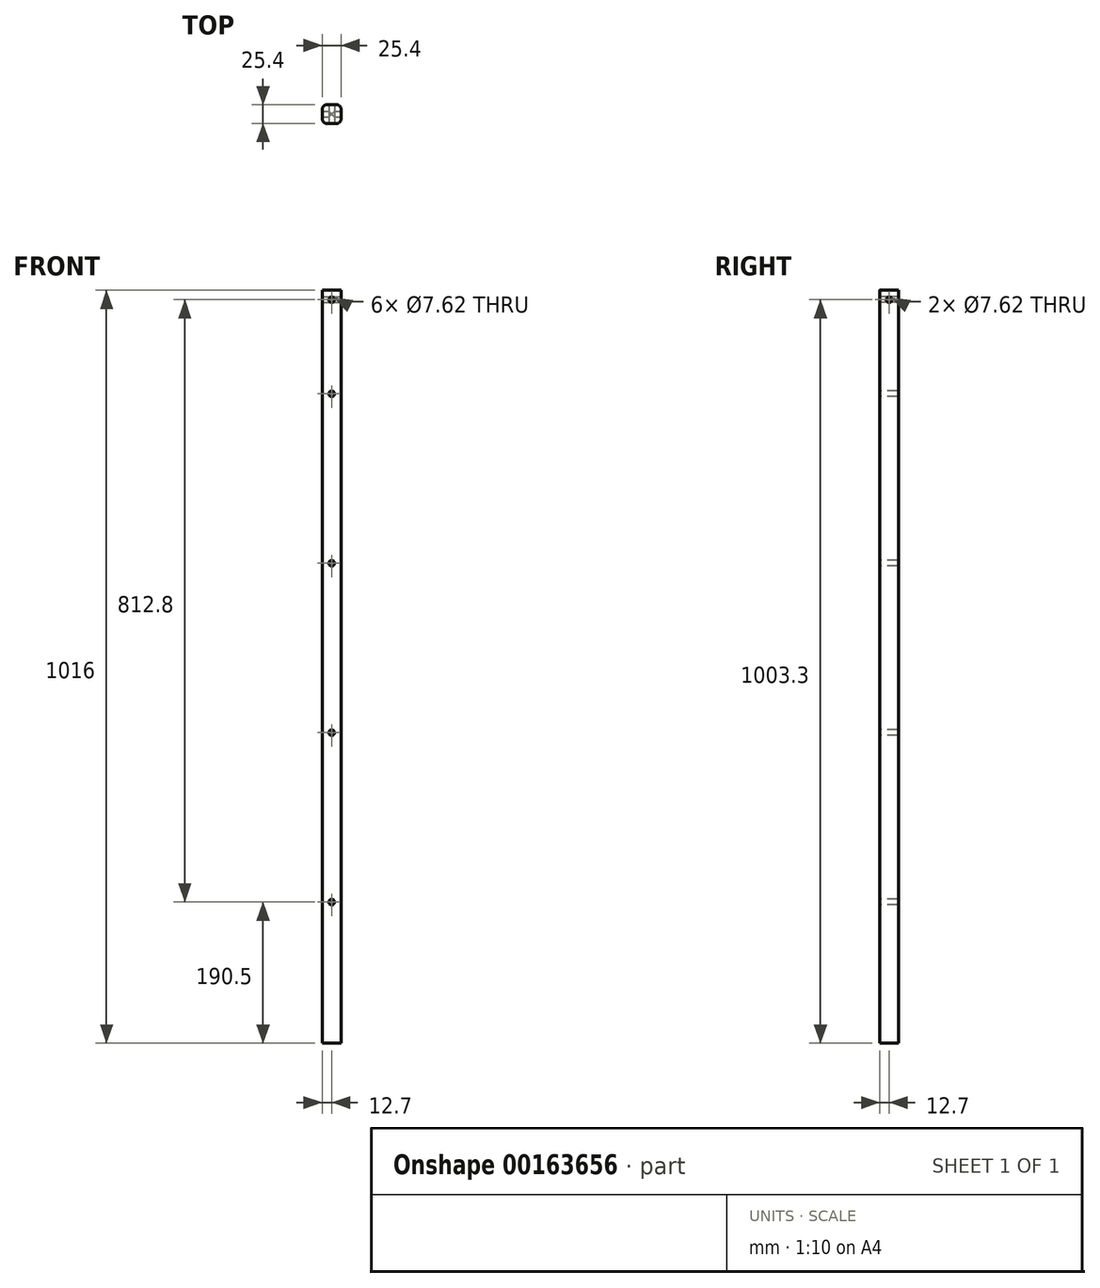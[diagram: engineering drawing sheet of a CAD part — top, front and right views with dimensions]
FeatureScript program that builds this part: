
annotation { "Feature Type Name" : "Feature", "Feature Type Description" : "" }
export const myFeature = defineFeature(function(context is Context, id is Id, definition is map)
    precondition{}
    {
        {
            var Q0;
            Q0=qCreatedBy(makeId("Top.planeOp"),FACE);
            var sketch = newSketch(context, id + "F0", { "sketchPlane" : qUnion([Q0])});
            skLineSegment(sketch, "E0.bottom", {"start": v(6.35, 12.7) * mm, "end": v(-6.35, 12.7) * mm});
            skLineSegment(sketch, "E0.top", {"start": v(6.35, -12.7) * mm, "end": v(-6.35, -12.7) * mm});
            skLineSegment(sketch, "E0.left", {"start": v(12.7, 6.35) * mm, "end": v(12.7, -6.35) * mm});
            skLineSegment(sketch, "E0.right", {"start": v(-12.7, 6.35) * mm, "end": v(-12.7, -6.35) * mm});
            skPoint(sketch, "E0.middle", {"position": v(0, 0) * mm});
            skPoint(sketch, "E1.visualSharp", {"position": v(-12.7, 12.7) * mm});
            skArc(sketch, "E1.filletArc", {"start": v(-6.35, 12.7) * mm, "mid": v(-10.84, 10.84) * mm, "end": v(-12.7, 6.35) * mm});
            skPoint(sketch, "E2.visualSharp", {"position": v(-12.7, -12.7) * mm});
            skArc(sketch, "E2.filletArc", {"start": v(-12.7, -6.35) * mm, "mid": v(-10.84, -10.84) * mm, "end": v(-6.35, -12.7) * mm});
            skPoint(sketch, "E3.visualSharp", {"position": v(12.7, -12.7) * mm});
            skArc(sketch, "E3.filletArc", {"start": v(6.35, -12.7) * mm, "mid": v(10.84, -10.84) * mm, "end": v(12.7, -6.35) * mm});
            skPoint(sketch, "E4.visualSharp", {"position": v(12.7, 12.7) * mm});
            skArc(sketch, "E4.filletArc", {"start": v(12.7, 6.35) * mm, "mid": v(10.84, 10.84) * mm, "end": v(6.35, 12.7) * mm});
            skSolve(sketch);
        }
        {
            var Q0;
            Q0=qSketchRegion(id+"F0",true);
            extrude(context, id + "F1", {"entities" : qUnion([Q0]), "depth" : 1016 * mm});
        }
        {
            var Q0;
            Q0=makeQuery(id+"F1.opExtrude","SWEPT_FACE",FACE,{"disambiguationData":[OSD([sQuery(id+"F0.wireOp",EDGE,"E0.top")])]});
            var sketch = newSketch(context, id + "F2", { "sketchPlane" : qUnion([Q0])});
            skLineSegment(sketch, "E5", {"start": v(0, 1016) * mm, "end": v(0, 1003.3) * mm});
            skPoint(sketch, "E5.endSnap0", {"position": v(0, 1016) * mm});
            skCircle(sketch, "E6", {"center": v(0, 1003.3) * mm, "radius": 3.81 * mm});
            skLineSegment(sketch, "E7", {"start": v(0, 1016) * mm, "end": v(0, 876.3) * mm, "construction": true});
            skLineSegment(sketch, "E8", {"start": v(0, 876.3) * mm, "end": v(0, 647.7) * mm, "construction": true});
            skCircle(sketch, "E9", {"center": v(0, 876.3) * mm, "radius": 3.81 * mm});
            skCircle(sketch, "E10", {"center": v(0, 647.7) * mm, "radius": 3.81 * mm});
            skLineSegment(sketch, "E11", {"start": v(0, 647.7) * mm, "end": v(0, 419.1) * mm, "construction": true});
            skCircle(sketch, "E12", {"center": v(0, 419.1) * mm, "radius": 3.81 * mm});
            skLineSegment(sketch, "E13", {"start": v(0, 0) * mm, "end": v(0, 190.5) * mm, "construction": true});
            skCircle(sketch, "E14", {"center": v(0, 190.5) * mm, "radius": 3.81 * mm});
            skSolve(sketch);
        }
        {
            var Q0;
            Q0=makeQuery(id+"F1.opExtrude","SWEPT_FACE",FACE,{"disambiguationData":[OSD([sQuery(id+"F0.wireOp",EDGE,"E0.left")])]});
            var sketch = newSketch(context, id + "F3", { "sketchPlane" : qUnion([Q0])});
            skPoint(sketch, "E15.endSnap0", {"position": v(0, 0) * mm});
            skLineSegment(sketch, "E16", {"start": v(0, 1016) * mm, "end": v(0, 1003.3) * mm});
            skPoint(sketch, "E16.endSnap0", {"position": v(0, 1016) * mm});
            skCircle(sketch, "E17", {"center": v(0, 1003.3) * mm, "radius": 3.81 * mm});
            skSolve(sketch);
        }
        {
            var Q0;
            Q0=makeQuery(id+"F3.imprint","IMPRINT",FACE,{"disambiguationData":[TD([[makeQuery(id+"F3.imprint","IMPRINT",EDGE,{"derivedFrom":sQuery(id+"F3.wireOp",EDGE,"E17")}),1.0]])]});
            var Q1;
            Q1=makeQuery(id+"F3.imprint","IMPRINT",FACE,{"disambiguationData":[TD([[makeQuery(id+"F3.imprint","IMPRINT",EDGE,{"derivedFrom":sQuery(id+"F3.wireOp",EDGE,"lmDfIelr-ZgLB-w0VR-bYfO-nWPvI039pRaW")}),1.0]])]});
            extrude(context, id + "F4", {"entities" : qUnion([Q0, Q1]), "operationType" : NewBodyOperationType.REMOVE, "oppositeDirection" : true, "depth" : 25.4 * mm});
        }
        {
            var Q0;
            Q0=makeQuery(id+"F2.imprint","IMPRINT",FACE,{"disambiguationData":[TD([[makeQuery(id+"F2.imprint","IMPRINT",EDGE,{"derivedFrom":sQuery(id+"F2.wireOp",EDGE,"E6")}),1.0]])]});
            var Q1;
            Q1=makeQuery(id+"F2.imprint","IMPRINT",FACE,{"disambiguationData":[TD([[makeQuery(id+"F2.imprint","IMPRINT",EDGE,{"derivedFrom":sQuery(id+"F2.wireOp",EDGE,"E9")}),1.0]])]});
            var Q2;
            Q2=makeQuery(id+"F2.imprint","IMPRINT",FACE,{"disambiguationData":[TD([[makeQuery(id+"F2.imprint","IMPRINT",EDGE,{"derivedFrom":sQuery(id+"F2.wireOp",EDGE,"E10")}),1.0]])]});
            var Q3;
            Q3=makeQuery(id+"F2.imprint","IMPRINT",FACE,{"disambiguationData":[TD([[makeQuery(id+"F2.imprint","IMPRINT",EDGE,{"derivedFrom":sQuery(id+"F2.wireOp",EDGE,"E12")}),1.0]])]});
            extrude(context, id + "F5", {"entities" : qUnion([Q0, Q1, Q2, Q3]), "operationType" : NewBodyOperationType.REMOVE, "oppositeDirection" : true, "depth" : 25.4 * mm, "offsetDistance" : 25.4 * mm});
        }
        {
            var Q0;
            Q0=makeQuery(id+"F2.imprint","IMPRINT",FACE,{"disambiguationData":[TD([[makeQuery(id+"F2.imprint","IMPRINT",EDGE,{"derivedFrom":sQuery(id+"F2.wireOp",EDGE,"E14")}),1.0]])]});
            extrude(context, id + "F6", {"entities" : qUnion([Q0]), "operationType" : NewBodyOperationType.REMOVE, "oppositeDirection" : true, "depth" : 25.4 * mm, "offsetDistance" : 25.4 * mm});
        }
    });
